# Revit family: Bosch-Boiler-GE615-Cast_Iron_Condensing_Boiler-141
name_source: partatom
category: Mechanical Equipment
revit_build: Autodesk Revit 2014 (Build: 20130308_1515(x64)
units: mm (PartAtom-declared; Revit-internal decimal feet)

## types (8) — shared parameters
6 Monthly = Service when oil fired
Access Clearance Bottom = 0
Access Clearance Left = 400 (depending on door handing)
Access Clearance Rear = 820
Access Clearance Right = Burner length + 100
Access Clearance Top = 0
Annually = Annual Service
Assembly Code = D3020100
AssetType = Fixed
BMS Links = Yes
Back (mm) = 1150 mm
Bespoke Timeframe = No
Burner Configuration = Separate
Burner D = 555 mm  [stored 1.82087 ft]
Burner E = 840 mm  [stored 2.75591 ft]
CE Approval = CE-0461 AU 417
ClassificationName = Uniclass2015
ClassificationValue = Pr_60_60_08_34
Color = Blue RAL classic 5015
Colour = Blue RAL classic 5015
Condensate Drain Type = Unset
Configuration = Single Boiler
Constituents = Cast Iron, steel, polymers
Control Options = Unset
Control Type = External
Daily = No
Description = The Buderus GE series includes a robust range of Ecostream boilers constructed from special Buderus GL 180 M grey cast iron which makes them extremely resistant to corrosion and high temperatures.
DocumentationInstallationGuide = https://specifi.bimstore.co.uk
DocumentationMaintenance = https://specifi.bimstore.co.uk
DocumentationTechnical = https://specifi.bimstore.co.uk
Drain Connection Size = R3/4"
Drain Connection Type = Threaded
DurationUnit = Years
ErP Energy Label = N
Expected Life = 20 - 30
ExpectedLife = 25
External Material = Steel
Features = High Efficiency Cast Iron Boiler
Finish = Paint
Flow and Return Connection Size = DN150
Flow and Return Connection Type = Flanged
Flue Connection Size = 360
Flue or Air Intake Classification = B23
Frequency = 50
Fuel Connection Type = Unset
Fuse Rating = 10
Heat Exchanger Material = Cast Iron
IP Rating = dependent on burner used
Interlocks = Yes
Keynote = T24/310
Left Side (mm) = 400 mm  [stored 1.31234 ft]
Maintenance Required 0-300hrs = No
Maintenance Required 1001-2000hrs = No
Maintenance Required 2001-4000hrs = No
Maintenance Required 301-600hrs = No
Maintenance Required 4001-8000hrs = No
Maintenance Required 601-1000hrs = No
Maintenance Required 8001-12000hrs = No
Manufacturer = Bosch Thermotechnology
Material = Cast Iron
Maximum Oil Inlet Pressure = 400
Maximum Operating Pressure = 6
Maximum Power Consumption = dependent on burner used
Minimum Oil Inlet Pressure = -0.40 (for twin pipe circuits)
Minimum Operating Pressure = 0.8
Minimum Power Consumption = dependent on burner used
Model = GE615 - Floor Standing Cast Iron High Efficiency Boiler
ModelNumber = GE615 - Floor Standing Cast Iron High Efficiency Boiler
Monthly = No
Mounting = Floor Standing
NBSObjectName = Gas fired condensing boilers
NBSReference = 90-40-05/340
Nominal Gas Inlet Pressure = 20
Nominal Oil Inlet Pressure = 50
O&M Manual = http://www.buderus.co.uk
Overall Height = 1826
Overall Width = 1281
Primary Fuel = Gas - NG
Product Literature = http://www.buderus.co.uk
Product Range = GE615
ProductionYear = 2015
Quaterly = No
Rated Criteria = 80/60
ReferencedStandard = BS EN
Room Height Min (mm) = 2500 mm  [stored 8.2021 ft]
Safety Valve Connection Size = DN65 (when using optional safety manifold)
Safety Valve Connection Type = Flanged
Secondary Fuel = Oil - 35/sec
Shape = Rectangular (Horizontal)
Supply Phase = 1ph - controls 3ph - burner
Turndown Ratio = dependent on burner used
Type = Space Heating
URL = http://www.buderus.co.uk
Voltage = 230 - controls 400 - burner
Warranty ID = Serial number and end user registration
WarrantyDurationUnit = Years
Weekly = System pressure check
Width = 1281 mm  [stored 4.20276 ft]
_current revision = 1
_distributed by = www.bimstore.co.uk
zero-valued in all types: _BIMspec_GUID

## per-type parameters (varying)
| type | Access Clearance Front | Building Regulations Seasonal Efficiency | Burner A | Front (mm) | Fuel Connection Size | Full Load Current | Gas Consumption rate | Gross Weight | Length | Maximum Gas Inlet Pressure | Minimum Gas Inlet Pressure | NOx Emissions | Oil Consumption rate | Overall Length | Rated Efficiency at Full Load | Rated Efficiency at Part Load | Rated Output | Right Side (mm) | Shipping Weight | Sound Pressure Level | Starting Current | Type Comments | TypeName | Water Content |
| 570kW | 2300 (1400 with shorter cleaning rods) | 86.3 | 511 mm | 2300 mm | R2" | 2.8 (dependent on burner used) | 64 | 3066 | 1926 mm | 25 | 16.9 (dependent on gas train used) | 128 - gas   160 - Oil | 52 | 1926 | 92.4 | 96.6 | 511 - 570 | 2026 mm | 2505 | 75 (dependent on burner) | 4.8 (dependent on burner used) | GE615 - 570kW | GE615 - 570kW | 561 |
| 660kW | 2300 (1400 with shorter cleaning rods) | 86.3 | 511 mm | 2300 mm | R2" | 2.8 (dependent on burner used) | 74 | 3368 | 2096 mm  [stored 6.87664 ft] | 25 | 16.4 (dependent on gas train used) | 128 - gas   160 - Oil | 60.3 | 2096 | 92.5 | 96.6 | 571 - 660 | 2196 mm  [stored 7.20472 ft] | 2747 | 75 (dependent on burner) | 4.8 (dependent on burner used) | GE615 - 660kW | GE615 - 660kW | 621 |
| 740kW | 2300 (1400 with shorter cleaning rods) | 86.4 | 527 mm  [stored 1.729 ft] | 2300 mm | R2" | 2.8 (dependent on burner used) | 83 | 3671 | 2266 mm  [stored 7.43438 ft] | 100 (dependent on gas train used) | 14.2 (dependent on gas train used) | 125 - gas   160 - Oil | 67.5 | 2266 | 92.5 | 96.7 | 661 - 740 | 2366 mm  [stored 7.76247 ft] | 2990 | 77 (dependent on burner) | 4.8 (dependent on burner used) | GE615 - 740kW | GE615 - 740kW | 681 |
| 820kW | 2300 (1400 with shorter cleaning rods) | 86.6 | 527 mm  [stored 1.729 ft] | 2300 mm | R2" | 3.3 (dependent on burner used) | 92 | 3973 | 2314 mm  [stored 7.59186 ft] | 100 (dependent on gas train used) | 17.3 (dependent on gas train used) | 125 - gas   160 - Oil | 74.9 | 2436 | 92.4 | 97 | 741 - 820 | 2414 mm  [stored 7.91995 ft] | 3232 | 77 (dependent on burner) | 5.9 (dependent on burner used) | GE615 - 820kW | GE615 - 820kW | 741 |
| 920kW | 3000 (1500 with shorter cleaning rods) | 86.6 | 553 mm  [stored 1.8143 ft] | 3000 mm  [stored 9.84252 ft] | R2" | 5.1 (dependent on burner used) | 103 | 4276 | 2606 mm  [stored 8.54987 ft] | 100 (dependent on gas train used) | 16.2 (dependent on gas train used) | 105 - gas   160 - Oil | 84 | 2606 | 92.4 | 97 | 821 - 920 | 2706 mm  [stored 8.87795 ft] | 3475 | 79 (dependent on burner) | 8.8 (dependent on burner used) | GE615 - 920kW | GE615 - 920kW | 801 |
| 1020kW | 3000 (1500 with shorter cleaning rods) | 86.6 | 553 mm  [stored 1.8143 ft] | 3000 mm  [stored 9.84252 ft] | R2" | 5.1 (dependent on burner used) | 114 | 4571 | 2776 mm  [stored 9.10761 ft] | 100 (dependent on gas train used) | 16.8 (dependent on gas train used) | 105 - gas   160 - Oil | 93 | 2776 | 92.4 | 97 | 921 - 1020 | 2876 mm  [stored 9.4357 ft] | 3710 | 79 (dependent on burner) | 8.8 (dependent on burner used) | GE615 - 1020kW | GE615 - 1020kW | 861 |
| 1110kW | 3000 (1500 with shorter cleaning rods) | 86.6 | 553 mm  [stored 1.8143 ft] | 3000 mm  [stored 9.84252 ft] | R2" | 5.1 (dependent on burner used) | 124 | 4879 | 2946 mm  [stored 9.66535 ft] | 100 (dependent on gas train used) | 16 (dependent on gas train used) | 105 - gas   160 - Oil | 101.3 | 2946 | 92.5 | 97 | 1021 - 1110 | 3046 mm  [stored 9.99344 ft] | 3953 | 79 (dependent on burner) | 8.8 (dependent on burner used) | GE615 - 1110kW | GE615 - 1110kW | 921 |
| 1200kW | 3000 (1500 with shorter cleaning rods) | 86.6 | 553 mm  [stored 1.8143 ft] | 3000 mm  [stored 9.84252 ft] | dependent on burner | 5.1 (dependent on burner used) | 134 | 5128 | 3116 mm  [stored 10.2231 ft] | 100 (dependent on gas train used) | 17.4 (dependent on gas train used) | 105 - gas   160 - Oil | 109.5 | 3116 | 92.5 | 97 | 1111 - 1200 | 3216 mm  [stored 10.5512 ft] | 4147 | 79 (dependent on burner) | 8.8 (dependent on burner used) | GE615 - 1200kW | GE615 - 1200kW | 981 |

note: column(s) folded — value = type name in every type: Product Model Number

note: [stored X ft] marks values corroborated as IEEE doubles in the binary element streams (Revit-internal decimal feet)

## geometry (parser evidence)
native form markers: Sweep x20
no freeform markers — native parametric forms only
